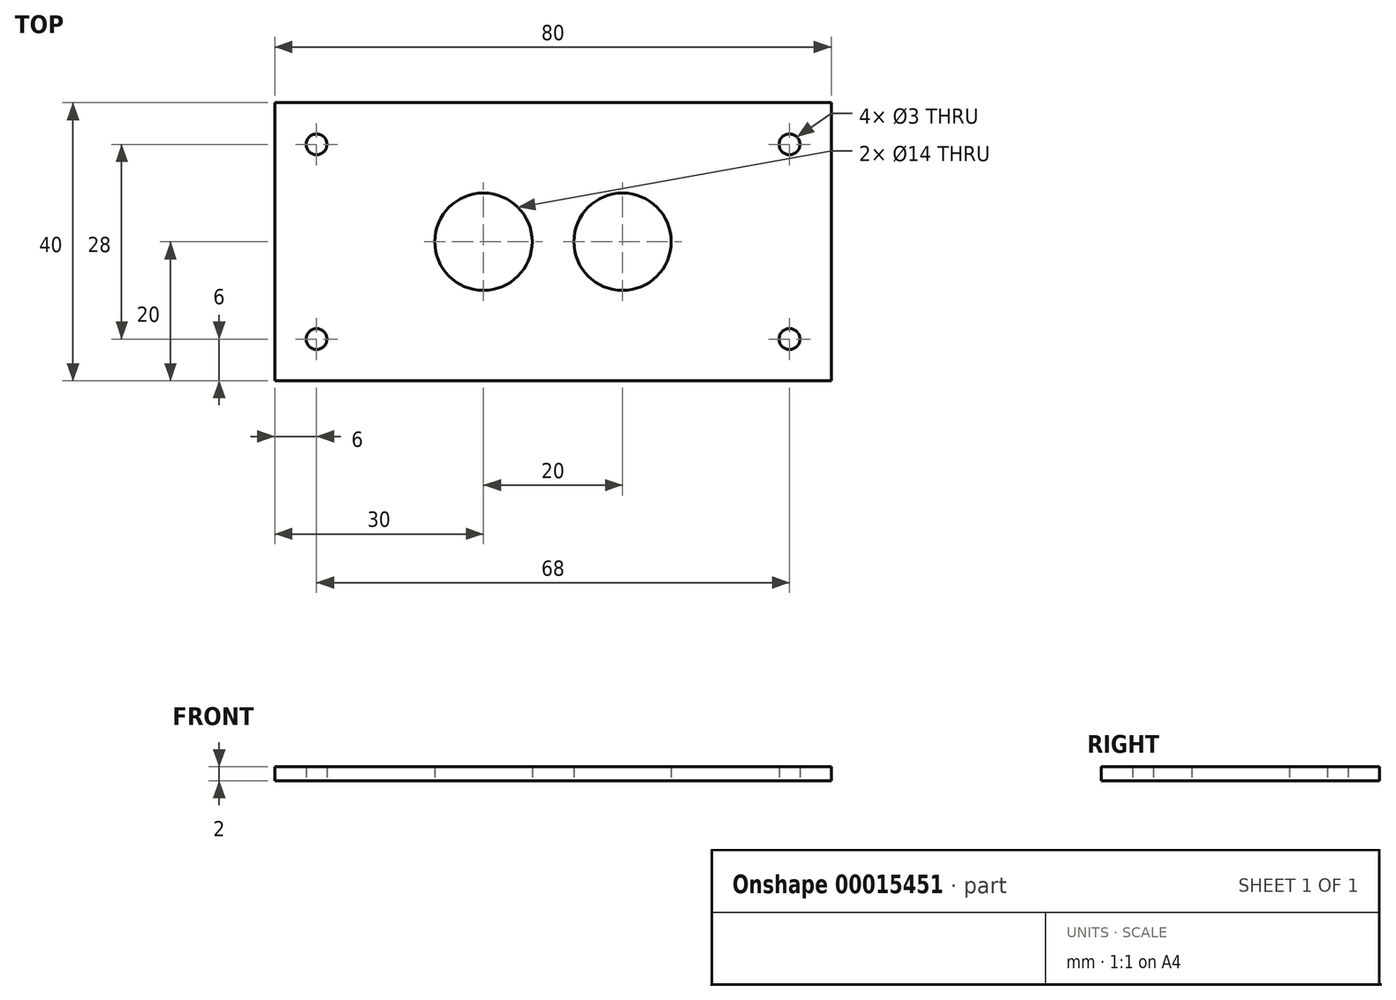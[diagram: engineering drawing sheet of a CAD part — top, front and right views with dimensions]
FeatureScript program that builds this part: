
annotation { "Feature Type Name" : "Feature", "Feature Type Description" : "" }
export const myFeature = defineFeature(function(context is Context, id is Id, definition is map)
    precondition{}
    {
        {
            var Q0;
            Q0=qCreatedBy(makeId("Top.planeOp"),FACE);
            var sketch = newSketch(context, id + "F0", { "sketchPlane" : qUnion([Q0])});
            skLineSegment(sketch, "E0.rect.bottom", {"start": v(40, 20) * mm, "end": v(-40, 20) * mm});
            skLineSegment(sketch, "E0.rect.right", {"start": v(-40, 20) * mm, "end": v(-40, -20) * mm});
            skLineSegment(sketch, "E1", {"start": v(-40, -20) * mm, "end": v(40, -20) * mm});
            skLineSegment(sketch, "E2", {"start": v(40, -20) * mm, "end": v(40, 20) * mm});
            skCircle(sketch, "E3", {"center": v(-10, 0) * mm, "radius": 7 * mm});
            skCircle(sketch, "E4", {"center": v(-34, 14) * mm, "radius": 6 * mm});
            skCircle(sketch, "E5", {"center": v(-34, 14) * mm, "radius": 1.5 * mm});
            skCircle(sketch, "E6", {"center": v(34, 14) * mm, "radius": 1.5 * mm});
            skCircle(sketch, "E7", {"center": v(34, 14) * mm, "radius": 6 * mm});
            skCircle(sketch, "E8", {"center": v(34, -14) * mm, "radius": 1.5 * mm});
            skCircle(sketch, "E9", {"center": v(34, -14) * mm, "radius": 6 * mm});
            skCircle(sketch, "E10", {"center": v(-34, -14) * mm, "radius": 1.5 * mm});
            skCircle(sketch, "E11", {"center": v(-34, -14) * mm, "radius": 6 * mm});
            skCircle(sketch, "E12", {"center": v(10, 0) * mm, "radius": 7 * mm});
            skSolve(sketch);
        }
        {
            var Q0;
            Q0 = qSketchRegion(id + "F0", true);
            extrude(context, id + "F1", {"entities" : qUnion([Q0]), "depth" : 2 * mm});
        }
    });
